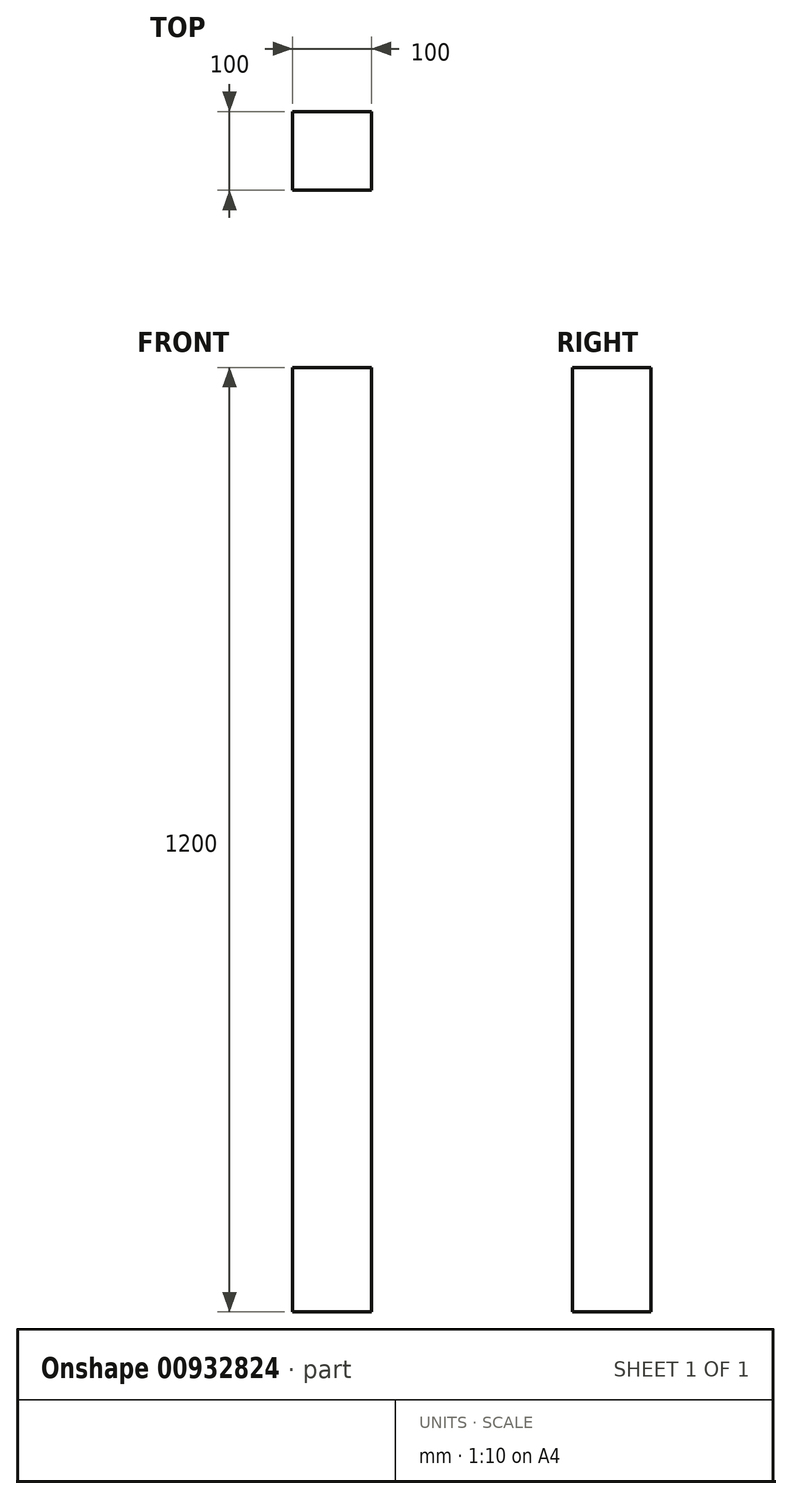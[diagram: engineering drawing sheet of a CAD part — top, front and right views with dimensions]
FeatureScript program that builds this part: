
annotation { "Feature Type Name" : "Feature", "Feature Type Description" : "" }
export const myFeature = defineFeature(function(context is Context, id is Id, definition is map)
    precondition{}
    {
        {
            var Q0;
            Q0=qCreatedBy(makeId("Top.planeOp"),FACE);
            var sketch = newSketch(context, id + "F0", { "sketchPlane" : qUnion([Q0])});
            skLineSegment(sketch, "E0.bottom", {"start": v(-50, 50) * mm, "end": v(50, 50) * mm});
            skLineSegment(sketch, "E0.top", {"start": v(-50, -50) * mm, "end": v(50, -50) * mm});
            skLineSegment(sketch, "E0.left", {"start": v(-50, 50) * mm, "end": v(-50, -50) * mm});
            skLineSegment(sketch, "E0.right", {"start": v(50, 50) * mm, "end": v(50, -50) * mm});
            skPoint(sketch, "E0.middle", {"position": v(0, 0) * mm});
            skSolve(sketch);
        }
        {
            var Q0;
            Q0 = qSketchRegion(id + "F0", true);
            extrude(context, id + "F1", {"entities" : qUnion([Q0]), "depth" : 1200 * mm, "offsetDistance" : 25 * mm, "symmetric" : true});
        }
    });
